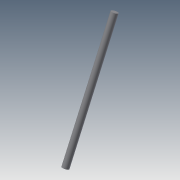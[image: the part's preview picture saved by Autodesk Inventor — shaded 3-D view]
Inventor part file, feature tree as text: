
AUTODESK INVENTOR PART (.ipt)
format: ipt  version: 2014 SP1 (Build 180222100, 222)  size: 107,520 bytes
history: native  units: in
note: dims shown in document units (in); Inventor stores cm internally (conversion verified against a paired STEP export)
features: extrude x3, sketch x3, reference x2
ambient origin geometry x8: Origin, YZ Plane, XZ Plane, XY Plane, X Axis, Y Axis, Z Axis, Center Point
bodies: Solid1 (feature_tree)
feature tree (8):
  extrude  "Extrusion1"  Depth=0.1649in
  extrude  "Extrusion2"  Depth=0.7874in TaperAngle=0.0deg
  extrude  "Extrusion3"  [1 undecoded]
  sketch  "Sketch1"  dims[d1=0.1649in d3=0.1649in]
  reference  "Reference1"
  reference  "Reference2"
  sketch  "Sketch2"  dims[d4=0.036in d5=0.0in d6=0.7874in d7=0.0in]
  sketch  "Sketch3"  dims[d8=0.3445in d9=0.0in]
note: 1 required parameter value undecoded (feature->parameter linkage not recoverable at this tier; creation-order binding heuristic only, values carry confidence <= 0.55)
